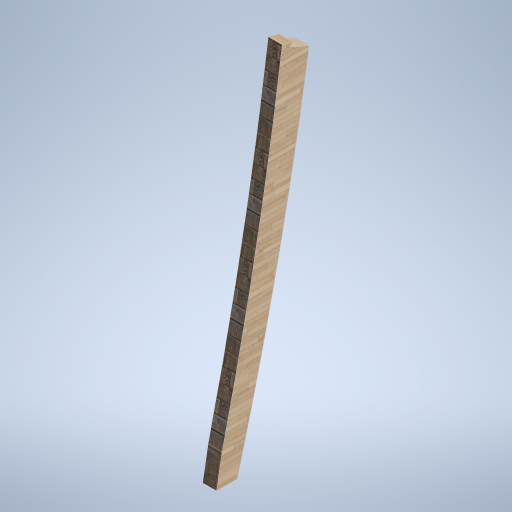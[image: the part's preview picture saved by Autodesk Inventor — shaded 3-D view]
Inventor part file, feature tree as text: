
AUTODESK INVENTOR PART (.ipt)
format: ipt  version: 2024.2 (Build 282272000, 272)  size: 318,976 bytes
history: native  units: in
note: dims shown in document units (in); Inventor stores cm internally (conversion verified against a paired STEP export)
features: other x3, sketch x1
ambient origin geometry x8: Origin, YZ Plane, XZ Plane, XY Plane, X Axis, Y Axis, Z Axis, Center Point
bodies: Solid1 (feature_tree)
feature tree (4):
  other  "side_curve_beam_02.ipt"
  other  "Solid1::side_curve_beam_02.ipt"
  other  "TaggingFeature1"
  sketch  "Sketch1"  dims[d0=0.3937in]
